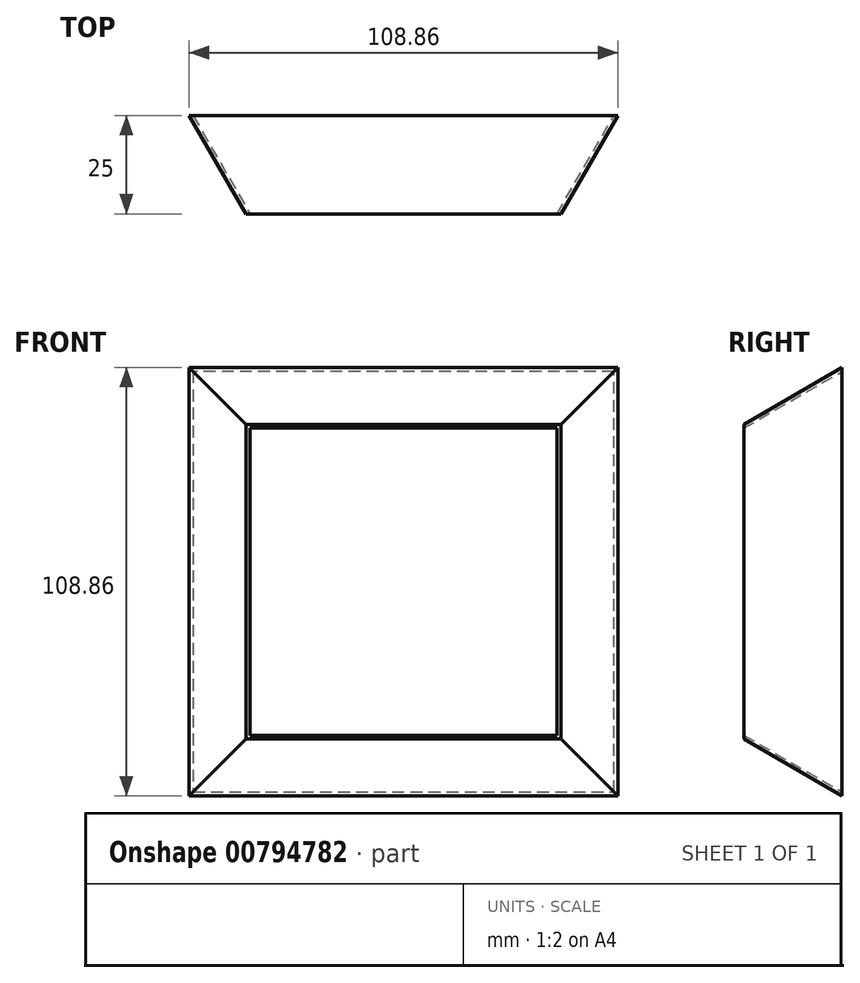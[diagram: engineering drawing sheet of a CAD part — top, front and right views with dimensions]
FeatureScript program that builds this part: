
annotation { "Feature Type Name" : "Feature", "Feature Type Description" : "" }
export const myFeature = defineFeature(function(context is Context, id is Id, definition is map)
    precondition{}
    {
        {
            var Q0;
            Q0=qCreatedBy(makeId("Front.planeOp"),FACE);
            var sketch = newSketch(context, id + "F0", { "sketchPlane" : qUnion([Q0])});
            skLineSegment(sketch, "E0.bottom", {"start": v(0, 0) * mm, "end": v(80, 0) * mm});
            skLineSegment(sketch, "E0.top", {"start": v(0, 80) * mm, "end": v(80, 80) * mm});
            skLineSegment(sketch, "E0.left", {"start": v(0, 0) * mm, "end": v(0, 80) * mm});
            skLineSegment(sketch, "E0.right", {"start": v(80, 0) * mm, "end": v(80, 80) * mm});
            skLineSegment(sketch, "E1.0", {"start": v(1, 79) * mm, "end": v(79, 79) * mm});
            skLineSegment(sketch, "E1.1", {"start": v(1, 1) * mm, "end": v(1, 79) * mm});
            skLineSegment(sketch, "E1.2", {"start": v(1, 1) * mm, "end": v(79, 1) * mm});
            skLineSegment(sketch, "E1.3", {"start": v(79, 1) * mm, "end": v(79, 79) * mm});
            skSolve(sketch);
        }
        {
            var Q0;
            Q0=makeQuery(id+"F0.imprint","IMPRINT",FACE,{"disambiguationData":[TD([[makeQuery(id+"F0.imprint","IMPRINT",EDGE,{"derivedFrom":sQuery(id+"F0.wireOp",EDGE,"E0.bottom")}),1.0]])]});
            var Q1;
            Q1=makeQuery(id+"F0.imprint","IMPRINT",FACE,{"disambiguationData":[TD([[makeQuery(id+"F0.imprint","IMPRINT",EDGE,{"derivedFrom":sQuery(id+"F0.wireOp",EDGE,"E1.0")}),-1.0]])]});
            extrude(context, id + "F1", {"entities" : qUnion([Q0, Q1]), "oppositeDirection" : true, "depth" : 25 * mm, "offsetDistance" : 25 * mm, "hasDraft" : true, "draftAngle" : 30 * degree});
        }
        {
            var Q0;
            Q0=makeQuery(id+"F0.imprint","IMPRINT",FACE,{"disambiguationData":[TD([[makeQuery(id+"F0.imprint","IMPRINT",EDGE,{"derivedFrom":sQuery(id+"F0.wireOp",EDGE,"E1.0")}),-1.0]])]});
            extrude(context, id + "F2", {"entities" : qUnion([Q0]), "operationType" : NewBodyOperationType.REMOVE, "oppositeDirection" : true, "depth" : 30 * mm, "offsetDistance" : 25 * mm, "hasDraft" : true, "draftAngle" : 30 * degree});
        }
    });
